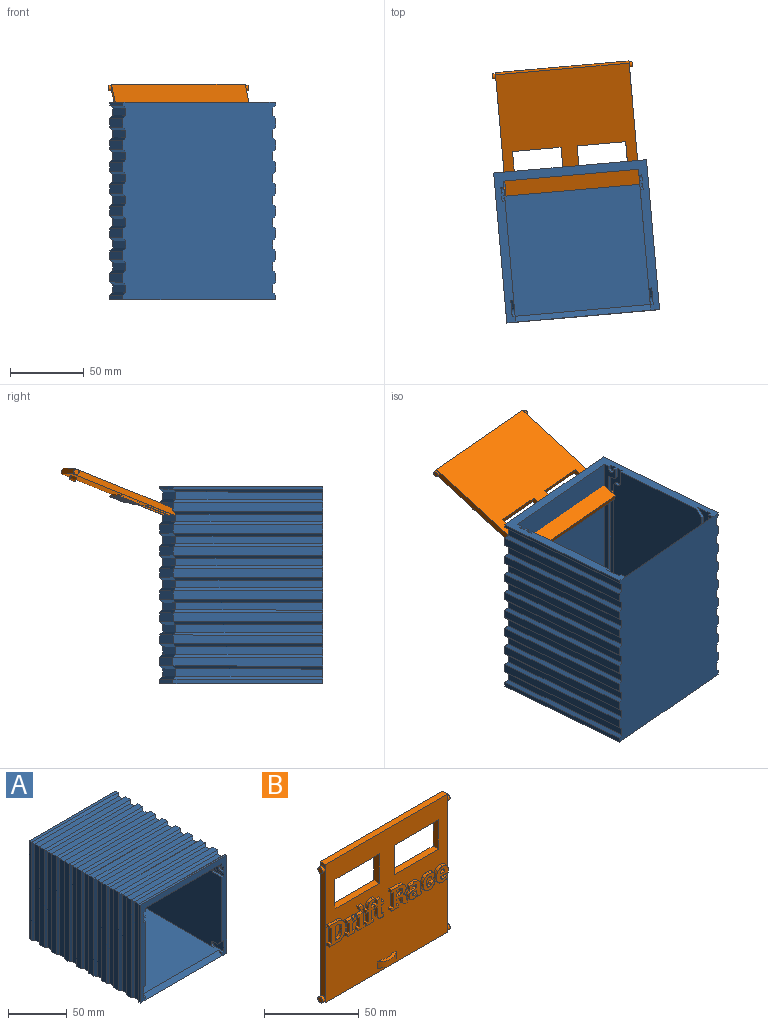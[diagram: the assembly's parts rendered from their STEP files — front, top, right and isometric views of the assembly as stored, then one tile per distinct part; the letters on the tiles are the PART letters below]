
ASSEMBLY  parts=2 mates=1
PART A: 160 faces, bbox 104x134x102 mm
  f0: plane 4x4mm, normal (-1,0,0), area 8mm2, adj f1,f32,f37
  f1: plane 104x102mm, normal (0,-1,0), area 1700mm2, adj f0,f2,f30,f32,f33,f34,f35,f38
  f2: plane 130x92mm, normal (1,0,0), area 11415.9mm2, adj f1,f32,f34,f36,f38,f39,f41,f42
  f3: plane 100x5mm, normal (0,0,1), area 500mm2, adj f12,f21,f134,f135
  f4: plane 100x5mm, normal (0,0,1), area 500mm2, adj f20,f22,f136,f137
  f5: plane 100x5mm, normal (0,0,1), area 500mm2, adj f19,f23,f138,f139
  f6: plane 100x5mm, normal (0,0,1), area 500mm2, adj f18,f24,f140,f141
  f7: plane 100x5mm, normal (0,0,1), area 500mm2, adj f17,f25,f142,f143
  f8: plane 100x5mm, normal (0,0,1), area 500mm2, adj f16,f26,f144,f145
  f9: plane 100x5mm, normal (0,0,1), area 500mm2, adj f13,f29,f150,f151
  f10: plane 100x5mm, normal (0,0,1), area 500mm2, adj f15,f27,f146,f147
  f11: plane 100x5mm, normal (0,0,1), area 500mm2, adj f14,f28,f148,f149
  f12: plane 100x5mm, normal (1,0,0), area 500mm2, adj f3,f30,f122,f123
  f13: plane 100x5mm, normal (1,0,0), area 500mm2, adj f9,f30,f106,f107
  f14: plane 100x5mm, normal (1,0,0), area 500mm2, adj f11,f30,f108,f109
  f15: plane 100x5mm, normal (1,0,0), area 500mm2, adj f10,f30,f110,f111
  f16: plane 100x5mm, normal (1,0,0), area 500mm2, adj f8,f30,f112,f113
  f17: plane 100x5mm, normal (1,0,0), area 500mm2, adj f7,f30,f114,f115
  f18: plane 100x5mm, normal (1,0,0), area 500mm2, adj f6,f30,f116,f117
  f19: plane 100x5mm, normal (1,0,0), area 500mm2, adj f5,f30,f118,f119
  f20: plane 100x5mm, normal (1,0,0), area 500mm2, adj f4,f30,f120,f121
  f21: plane 100x5mm, normal (-1,0,0), area 500mm2, adj f3,f30,f79,f80
  f22: plane 100x5mm, normal (-1,0,0), area 500mm2, adj f4,f30,f81,f82
  f23: plane 100x5mm, normal (-1,0,0), area 500mm2, adj f5,f30,f83,f84
  f24: plane 100x5mm, normal (-1,0,0), area 500mm2, adj f6,f30,f85,f86
  f25: plane 100x5mm, normal (-1,0,0), area 500mm2, adj f7,f30,f87,f88
  f26: plane 100x5mm, normal (-1,0,0), area 500mm2, adj f8,f30,f89,f90
  f27: plane 100x5mm, normal (-1,0,0), area 500mm2, adj f10,f30,f91,f92
  f28: plane 100x5mm, normal (-1,0,0), area 500mm2, adj f11,f30,f93,f94
  f29: plane 100x5mm, normal (-1,0,0), area 500mm2, adj f9,f30,f78,f95
  f30: plane 134x104mm, normal (0,0,-1), area 13684mm2, adj f1,f12,f13,f14,f15,f16,f17,f18
  f31: plane 104x102mm, normal (0,1,0), area 10608mm2, adj f30,f68,f104,f126
  f32: plane 130x96mm, normal (0,0,1), area 11632mm2, adj f0,f1,f2,f33,f35,f36,f37,f153
  f33: plane 4x4mm, normal (1,0,0), area 8mm2, adj f1,f32,f37
  f34: plane 130x92mm, normal (0,0,-1), area 11960mm2, adj f1,f2,f35,f36
  f35: plane 130x92mm, normal (-1,0,0), area 11431.9mm2, adj f1,f32,f34,f36,f48,f49,f51,f52
  f36: plane 92x92mm, normal (0,-1,0), area 8464mm2, adj f2,f32,f34,f35
  f37: plane 92x4mm, normal (0,-0.71,0.71), area 520.4mm2, adj f0,f30,f32,f33
  f38: plane 2x2mm, normal (0,0,1), area 4mm2, adj f1,f2,f40,f67
  f39: plane 2x2mm, normal (0,0,-1), area 4mm2, adj f1,f2,f40,f67
  f40: plane 4x4mm, normal (1,0,0), area 14.3mm2, adj f1,f38,f39,f67
  f41: plane 2x2mm, normal (0,-1,0), area 4mm2, adj f2,f47,f64,f65
  f42: plane 89x2mm, normal (0,0,1), area 178mm2, adj f2,f47,f65,f66
  f43: plane 95x2mm, normal (0,0,-1), area 190mm2, adj f2,f44,f47,f66
  f44: plane 4x2mm, normal (0,1,0), area 8mm2, adj f2,f43,f47,f63
  f45: plane 6x2mm, normal (0,0,-1), area 12mm2, adj f1,f2,f47,f63
  f46: plane 10x2mm, normal (0,0,1), area 20mm2, adj f1,f2,f47,f64
  f47: plane 105x10mm, normal (1,0,0), area 443.1mm2, adj f1,f41,f42,f43,f44,f45,f46,f63
  f48: plane 2x2mm, normal (0,0,-1), area 4mm2, adj f1,f35,f50,f62
  f49: plane 2x2mm, normal (0,0,1), area 4mm2, adj f1,f35,f50,f62
  f50: plane 4x4mm, normal (-1,0,0), area 14.3mm2, adj f1,f48,f49,f62
  f51: plane 4x2mm, normal (0,1,0), area 8mm2, adj f35,f52,f57,f60
  f52: plane 91x2mm, normal (0,0,-1), area 182mm2, adj f35,f51,f57,f58
  f53: plane 85x2mm, normal (0,0,1), area 170mm2, adj f35,f57,f58,f59
  f54: plane 2x2mm, normal (0,-1,0), area 4mm2, adj f35,f57,f59,f61
  f55: plane 10x2mm, normal (0,0,1), area 20mm2, adj f1,f35,f57,f61
  f56: plane 6x2mm, normal (0,0,-1), area 12mm2, adj f1,f35,f57,f60
  f57: plane 101x10mm, normal (-1,0,0), area 427.1mm2, adj f1,f51,f52,f53,f54,f55,f56,f58
  f58: cylinder r=2mm len=4mm, axis (-1,0,0), area 12.6mm2, adj f35,f52,f53,f57
  f59: cylinder r=2mm len=2mm, axis (1,0,0), area 6.3mm2, adj f35,f53,f54,f57
  f60: cylinder r=2mm len=2mm, axis (-1,0,0), area 6.3mm2, adj f35,f51,f56,f57
  f61: cylinder r=2mm len=2mm, axis (1,0,0), area 6.3mm2, adj f35,f54,f55,f57
  f62: cylinder r=2mm len=4mm, axis (1,0,0), area 12.6mm2, adj f35,f48,f49,f50
  f63: cylinder r=2mm len=2mm, axis (-1,0,0), area 6.3mm2, adj f2,f44,f45,f47
  f64: cylinder r=2mm len=2mm, axis (-1,0,0), area 6.3mm2, adj f2,f41,f46,f47
  f65: cylinder r=2mm len=2mm, axis (-1,0,0), area 6.3mm2, adj f2,f41,f42,f47
  f66: cylinder r=2mm len=4mm, axis (-1,0,0), area 12.6mm2, adj f2,f42,f43,f47
  f67: cylinder r=2mm len=4mm, axis (-1,0,0), area 12.6mm2, adj f2,f38,f39,f40
  f68: plane 102x3mm, normal (-1,0,0), area 306mm2, adj f30,f31,f78,f126
  f69: plane 102x6mm, normal (-1,0,0), area 612mm2, adj f30,f94,f95,f124
  f70: plane 102x6mm, normal (-1,0,0), area 612mm2, adj f30,f92,f93,f125
  f71: plane 102x6mm, normal (-1,0,0), area 612mm2, adj f30,f90,f91,f127
  f72: plane 102x6mm, normal (-1,0,0), area 612mm2, adj f30,f88,f89,f128
  f73: plane 102x6mm, normal (-1,0,0), area 612mm2, adj f30,f86,f87,f129
  f74: plane 102x6mm, normal (-1,0,0), area 612mm2, adj f30,f84,f85,f130
  f75: plane 102x6mm, normal (-1,0,0), area 612mm2, adj f30,f82,f83,f131
  f76: plane 102x6mm, normal (-1,0,0), area 612mm2, adj f30,f80,f81,f132
  f77: plane 102x2mm, normal (-1,0,0), area 204mm2, adj f1,f30,f79,f133
  f78: plane 102x2mm, normal (-0.71,-0.71,0), area 285.7mm2, adj f29,f30,f68,f151
  f79: plane 102x2mm, normal (-0.71,0.71,0), area 285.7mm2, adj f21,f30,f77,f134
  f80: plane 102x2mm, normal (-0.71,-0.71,0), area 285.7mm2, adj f21,f30,f76,f135
  f81: plane 102x2mm, normal (-0.71,0.71,0), area 285.7mm2, adj f22,f30,f76,f136
  f82: plane 102x2mm, normal (-0.71,-0.71,0), area 285.7mm2, adj f22,f30,f75,f137
  f83: plane 102x2mm, normal (-0.71,0.71,0), area 285.7mm2, adj f23,f30,f75,f138
  f84: plane 102x2mm, normal (-0.71,-0.71,0), area 285.7mm2, adj f23,f30,f74,f139
  f85: plane 102x2mm, normal (-0.71,0.71,0), area 285.7mm2, adj f24,f30,f74,f140
  f86: plane 102x2mm, normal (-0.71,-0.71,0), area 285.7mm2, adj f24,f30,f73,f141
  f87: plane 102x2mm, normal (-0.71,0.71,0), area 285.7mm2, adj f25,f30,f73,f142
  f88: plane 102x2mm, normal (-0.71,-0.71,0), area 285.7mm2, adj f25,f30,f72,f143
  f89: plane 102x2mm, normal (-0.71,0.71,0), area 285.7mm2, adj f26,f30,f72,f144
  f90: plane 102x2mm, normal (-0.71,-0.71,0), area 285.7mm2, adj f26,f30,f71,f145
  f91: plane 102x2mm, normal (-0.71,0.71,0), area 285.7mm2, adj f27,f30,f71,f146
  f92: plane 102x2mm, normal (-0.71,-0.71,0), area 285.7mm2, adj f27,f30,f70,f147
  f93: plane 102x2mm, normal (-0.71,0.71,0), area 285.7mm2, adj f28,f30,f70,f148
  f94: plane 102x2mm, normal (-0.71,-0.71,0), area 285.7mm2, adj f28,f30,f69,f149
  f95: plane 102x2mm, normal (-0.71,0.71,0), area 285.7mm2, adj f29,f30,f69,f150
  f96: plane 102x6mm, normal (1,0,0), area 612mm2, adj f30,f121,f122,f132
  f97: plane 102x6mm, normal (1,0,0), area 612mm2, adj f30,f119,f120,f131
  f98: plane 102x6mm, normal (1,0,0), area 612mm2, adj f30,f117,f118,f130
  f99: plane 102x6mm, normal (1,0,0), area 612mm2, adj f30,f115,f116,f129
  f100: plane 102x6mm, normal (1,0,0), area 612mm2, adj f30,f113,f114,f128
  f101: plane 102x6mm, normal (1,0,0), area 612mm2, adj f30,f111,f112,f127
  f102: plane 102x6mm, normal (1,0,0), area 612mm2, adj f30,f109,f110,f125
  f103: plane 102x6mm, normal (1,0,0), area 612mm2, adj f30,f106,f108,f124
  f104: plane 102x3mm, normal (1,0,0), area 306mm2, adj f30,f31,f107,f126
  f105: plane 102x2mm, normal (1,0,0), area 204mm2, adj f1,f30,f123,f133
  f106: plane 102x2mm, normal (0.71,0.71,0), area 285.7mm2, adj f13,f30,f103,f150
  f107: plane 102x2mm, normal (0.71,-0.71,0), area 285.7mm2, adj f13,f30,f104,f151
  f108: plane 102x2mm, normal (0.71,-0.71,0), area 285.7mm2, adj f14,f30,f103,f149
  f109: plane 102x2mm, normal (0.71,0.71,0), area 285.7mm2, adj f14,f30,f102,f148
  f110: plane 102x2mm, normal (0.71,-0.71,0), area 285.7mm2, adj f15,f30,f102,f147
  f111: plane 102x2mm, normal (0.71,0.71,0), area 285.7mm2, adj f15,f30,f101,f146
  f112: plane 102x2mm, normal (0.71,-0.71,0), area 285.7mm2, adj f16,f30,f101,f145
  f113: plane 102x2mm, normal (0.71,0.71,0), area 285.7mm2, adj f16,f30,f100,f144
  f114: plane 102x2mm, normal (0.71,-0.71,0), area 285.7mm2, adj f17,f30,f100,f143
  f115: plane 102x2mm, normal (0.71,0.71,0), area 285.7mm2, adj f17,f30,f99,f142
  f116: plane 102x2mm, normal (0.71,-0.71,0), area 285.7mm2, adj f18,f30,f99,f141
  f117: plane 102x2mm, normal (0.71,0.71,0), area 285.7mm2, adj f18,f30,f98,f140
  f118: plane 102x2mm, normal (0.71,-0.71,0), area 285.7mm2, adj f19,f30,f98,f139
  f119: plane 102x2mm, normal (0.71,0.71,0), area 285.7mm2, adj f19,f30,f97,f138
  f120: plane 102x2mm, normal (0.71,-0.71,0), area 285.7mm2, adj f20,f30,f97,f137
  f121: plane 102x2mm, normal (0.71,0.71,0), area 285.7mm2, adj f20,f30,f96,f136
  f122: plane 102x2mm, normal (0.71,-0.71,0), area 285.7mm2, adj f12,f30,f96,f135
  f123: plane 102x2mm, normal (0.71,0.71,0), area 285.7mm2, adj f12,f30,f105,f134
  f124: plane 104x6mm, normal (0,0,1), area 624mm2, adj f69,f103,f149,f150
  f125: plane 104x6mm, normal (0,0,1), area 624mm2, adj f70,f102,f147,f148
  f126: plane 104x3mm, normal (0,0,1), area 312mm2, adj f31,f68,f104,f151
  f127: plane 104x6mm, normal (0,0,1), area 624mm2, adj f71,f101,f145,f146
  f128: plane 104x6mm, normal (0,0,1), area 624mm2, adj f72,f100,f143,f144
  f129: plane 104x6mm, normal (0,0,1), area 624mm2, adj f73,f99,f141,f142
  f130: plane 104x6mm, normal (0,0,1), area 624mm2, adj f74,f98,f139,f140
  f131: plane 104x6mm, normal (0,0,1), area 624mm2, adj f75,f97,f137,f138
  f132: plane 104x6mm, normal (0,0,1), area 624mm2, adj f76,f96,f135,f136
  f133: plane 104x2mm, normal (0,0,1), area 208mm2, adj f1,f77,f105,f134
  f134: plane 104x2mm, normal (0,0.71,0.71), area 288.5mm2, adj f3,f79,f123,f133
  f135: plane 104x2mm, normal (0,-0.71,0.71), area 288.5mm2, adj f3,f80,f122,f132
  f136: plane 104x2mm, normal (0,0.71,0.71), area 288.5mm2, adj f4,f81,f121,f132
  f137: plane 104x2mm, normal (0,-0.71,0.71), area 288.5mm2, adj f4,f82,f120,f131
  f138: plane 104x2mm, normal (0,0.71,0.71), area 288.5mm2, adj f5,f83,f119,f131
  f139: plane 104x2mm, normal (0,-0.71,0.71), area 288.5mm2, adj f5,f84,f118,f130
  f140: plane 104x2mm, normal (0,0.71,0.71), area 288.5mm2, adj f6,f85,f117,f130
  f141: plane 104x2mm, normal (0,-0.71,0.71), area 288.5mm2, adj f6,f86,f116,f129
  f142: plane 104x2mm, normal (0,0.71,0.71), area 288.5mm2, adj f7,f87,f115,f129
  f143: plane 104x2mm, normal (0,-0.71,0.71), area 288.5mm2, adj f7,f88,f114,f128
  f144: plane 104x2mm, normal (0,0.71,0.71), area 288.5mm2, adj f8,f89,f113,f128
  f145: plane 104x2mm, normal (0,-0.71,0.71), area 288.5mm2, adj f8,f90,f112,f127
  f146: plane 104x2mm, normal (0,0.71,0.71), area 288.5mm2, adj f10,f91,f111,f127
  f147: plane 104x2mm, normal (0,-0.71,0.71), area 288.5mm2, adj f10,f92,f110,f125
  f148: plane 104x2mm, normal (0,0.71,0.71), area 288.5mm2, adj f11,f93,f109,f125
  f149: plane 104x2mm, normal (0,-0.71,0.71), area 288.5mm2, adj f11,f94,f108,f124
  f150: plane 104x2mm, normal (0,0.71,0.71), area 288.5mm2, adj f9,f95,f106,f124
  f151: plane 104x2mm, normal (0,-0.71,0.71), area 288.5mm2, adj f9,f78,f107,f126
  f152: plane 5x2mm, normal (0,0,-1), area 10mm2, adj f2,f153,f157,f159
  f153: plane 13x11mm, normal (1,0,0), area 86.6mm2, adj f1,f32,f152,f157,f159
  f154: plane 5x2mm, normal (0,0,-1), area 10mm2, adj f35,f155,f156,f158
  f155: plane 13x11mm, normal (-1,0,0), area 86.6mm2, adj f1,f32,f154,f156,f158
  f156: cylinder r=3mm len=6mm, axis (-1,0,0), area 18.8mm2, adj f32,f35,f154,f155
  f157: cylinder r=3mm len=6mm, axis (-1,0,0), area 18.8mm2, adj f2,f32,f152,f153
  f158: plane 5x5mm, normal (0,-0.71,-0.71), area 14.1mm2, adj f1,f35,f154,f155
  f159: plane 5x5mm, normal (0,-0.71,-0.71), area 14.1mm2, adj f1,f2,f152,f153
PART B: 254 faces, bbox 95x7x89 mm
  f0: plane 14x3mm, normal (0,0,-1), area 23.9mm2, adj f2,f251,f252
  f1: plane 14x3mm, normal (0,0,1), area 23.9mm2, adj f2,f251,f252
  f2: plane 91x89mm, normal (0,-1,0), area 6218mm2, adj f0,f1,f4,f5,f6,f22,f23,f24
  f3: plane 91x89mm, normal (0,1,0), area 6845mm2, adj f4,f5,f6,f243,f244,f245,f246,f247
  f4: plane 89x4mm, normal (1,0,0), area 336.8mm2, adj f2,f3,f6,f9,f13,f253
  f5: plane 89x4mm, normal (-1,0,0), area 336.8mm2, adj f2,f3,f6,f8,f12,f253
  f6: plane 91x4mm, normal (0,0,-1), area 364mm2, adj f2,f3,f4,f5
  f7: plane 3.5x3.5mm, normal (-1,0,0), area 9.6mm2, adj f8
  f8: cylinder r=1.75mm len=3.5mm, axis (1,0,0), area 22mm2, adj f5,f7
  f9: cylinder r=1.75mm len=3.5mm, axis (1,0,0), area 22mm2, adj f4,f10
  f10: plane 3.5x3.5mm, normal (1,0,0), area 9.6mm2, adj f9
  f11: plane 3.5x3.5mm, normal (-1,0,0), area 9.6mm2, adj f12
  f12: cylinder r=1.75mm len=3.5mm, axis (1,0,0), area 22mm2, adj f5,f11
  f13: cylinder r=1.75mm len=3.5mm, axis (1,0,0), area 22mm2, adj f4,f14
  f14: plane 3.5x3.5mm, normal (1,0,0), area 9.6mm2, adj f13
  f15: plane 9.33x2mm, normal (1,0,0), area 18.7mm2, adj f16,f34,f35,f36
  f16: plane 2x1.79mm, normal (0,0,-1), area 3.6mm2, adj f15,f17,f35,f36
  f17: extruded ~2.28x2mm, area 5.1mm2, adj f16,f18,f35,f36
  f18: extruded ~2.55x2mm, area 5.5mm2, adj f17,f19,f35,f36
  f19: plane 2.25x2mm, normal (-1,0,0), area 4.5mm2, adj f18,f20,f35,f36
  f20: extruded ~2.57x2mm, area 5.5mm2, adj f19,f21,f35,f36
  f21: extruded ~2.28x2mm, area 5.1mm2, adj f20,f34,f35,f36
  f22: extruded ~4.08x2mm, area 9mm2, adj f2,f23,f33,f35
  f23: plane 6.07x2mm, normal (0,0,1), area 12.1mm2, adj f2,f22,f24,f35
  f24: plane 2x1.63mm, normal (-1,0,0), area 3.3mm2, adj f2,f23,f25,f35
  f25: plane 2x1.44mm, normal (-0.19,0,-0.98), area 2.9mm2, adj f2,f24,f26,f35
  f26: plane 9.68x2mm, normal (-1,0,0), area 19.4mm2, adj f2,f25,f27,f35
  f27: plane 2x1.44mm, normal (-0.19,0,0.98), area 2.9mm2, adj f2,f26,f28,f35
  f28: plane 2x1.62mm, normal (-1,0,0), area 3.2mm2, adj f2,f27,f29,f35
  f29: plane 6.07x2mm, normal (0,0,-1), area 12.1mm2, adj f2,f28,f30,f35
  f30: extruded ~4.08x2mm, area 9mm2, adj f2,f29,f31,f35
  f31: extruded ~4.05x2mm, area 9mm2, adj f2,f30,f32,f35
  f32: plane 2.23x2mm, normal (1,0,0), area 4.5mm2, adj f2,f31,f33,f35
  f33: extruded ~4.05x2mm, area 9mm2, adj f2,f22,f32,f35
  f34: plane 2x1.79mm, normal (0,0,1), area 3.6mm2, adj f15,f21,f35,f36
  f35: plane 13.49x11.75mm, normal (0,-1,0), area 90mm2, adj f15,f16,f17,f18,f19,f20,f21,f22
  f36: plane 9.33x4.89mm, normal (0,-1,0), area 41.5mm2, adj f15,f16,f17,f18,f19,f20,f21,f34
  f37: plane 2x1.3mm, normal (-0.21,0,0.98), area 2.7mm2, adj f2,f38,f55,f56
  f38: plane 2x1.62mm, normal (-1,0,0), area 3.2mm2, adj f2,f37,f39,f56
  f39: plane 5.3x2mm, normal (0,0,-1), area 10.6mm2, adj f2,f38,f40,f56
  f40: plane 2x1.62mm, normal (1,0,0), area 3.2mm2, adj f2,f39,f41,f56
  f41: plane 2x1.3mm, normal (0.21,0,0.98), area 2.7mm2, adj f2,f40,f42,f56
  f42: plane 4.87x2mm, normal (1,0,0), area 9.7mm2, adj f2,f41,f43,f56
  f43: extruded ~2x0.66mm, area 1.8mm2, adj f2,f42,f44,f56
  f44: extruded ~2x0.98mm, area 2mm2, adj f2,f43,f45,f56
  f45: plane 2x1.11mm, normal (-0.02,0,-1), area 2.2mm2, adj f2,f44,f46,f56
  f46: plane 2.46x2mm, normal (0.99,0,-0.12), area 5mm2, adj f2,f45,f47,f56
  f47: extruded ~2x0.39mm, area 0.8mm2, adj f2,f46,f48,f56
  f48: extruded ~2x0.45mm, area 0.9mm2, adj f2,f47,f49,f56
  f49: extruded ~2x1.29mm, area 2.8mm2, adj f2,f48,f50,f56
  f50: extruded ~2x1.21mm, area 3.1mm2, adj f2,f49,f51,f56
  f51: plane 2x1.46mm, normal (1,0,0.08), area 2.9mm2, adj f2,f50,f52,f56
  f52: plane 3.95x2mm, normal (0,0,1), area 7.9mm2, adj f2,f51,f53,f56
  f53: plane 2x1.63mm, normal (-1,0,0), area 3.3mm2, adj f2,f52,f54,f56
  f54: plane 2x1.44mm, normal (-0.19,0,-0.98), area 2.9mm2, adj f2,f53,f55,f56
  f55: plane 6.22x2mm, normal (-1,0,0), area 12.4mm2, adj f2,f37,f54,f56
  f56: plane 10.21x7.12mm, normal (0,-1,0), area 40.7mm2, adj f37,f38,f39,f40,f41,f42,f43,f44
  f57: plane 2x1.3mm, normal (-0.21,0,0.98), area 2.7mm2, adj f2,f58,f66,f67
  f58: plane 2x1.62mm, normal (-1,0,0), area 3.2mm2, adj f2,f57,f59,f67
  f59: plane 5.31x2mm, normal (0,0,-1), area 10.6mm2, adj f2,f58,f60,f67
  f60: plane 2x1.62mm, normal (1,0,0), area 3.2mm2, adj f2,f59,f61,f67
  f61: plane 2x1.3mm, normal (0.21,0,0.98), area 2.7mm2, adj f2,f60,f62,f67
  f62: plane 8.12x2mm, normal (1,0,0), area 16.2mm2, adj f2,f61,f63,f67
  f63: plane 4.15x2mm, normal (0,0,1), area 8.3mm2, adj f2,f62,f64,f67
  f64: plane 2x1.63mm, normal (-1,0,0), area 3.3mm2, adj f2,f63,f65,f67
  f65: plane 2x1.44mm, normal (-0.19,0,-0.98), area 2.9mm2, adj f2,f64,f66,f67
  f66: plane 6.22x2mm, normal (-1,0,0), area 12.4mm2, adj f2,f57,f65,f67
  f67: plane 10.02x5.45mm, normal (0,-1,0), area 34.3mm2, adj f57,f58,f59,f60,f61,f62,f63,f64
  f68: plane 2.71x2mm, normal (0,0,-1), area 5.4mm2, adj f2,f69,f71,f72
  f69: plane 2.03x2mm, normal (1,0,0), area 4.1mm2, adj f2,f68,f70,f72
  f70: plane 2.71x2mm, normal (0,0,1), area 5.4mm2, adj f2,f69,f71,f72
  f71: plane 2.03x2mm, normal (-1,0,0), area 4.1mm2, adj f2,f68,f70,f72
  f72: plane 2.71x2.03mm, normal (0,-1,0), area 5.5mm2, adj f68,f69,f70,f71
  f73: plane 2x1.31mm, normal (-0.21,0,0.98), area 2.7mm2, adj f2,f74,f96,f97
  f74: plane 2x1.62mm, normal (-1,0,0), area 3.2mm2, adj f2,f73,f75,f97
  f75: plane 5.32x2mm, normal (0,0,-1), area 10.6mm2, adj f2,f74,f76,f97
  f76: plane 2x1.62mm, normal (1,0,0), area 3.2mm2, adj f2,f75,f77,f97
  f77: plane 2x1.31mm, normal (0.21,0,0.98), area 2.7mm2, adj f2,f76,f78,f97
  f78: plane 6.23x2mm, normal (1,0,0), area 12.5mm2, adj f2,f77,f79,f97
  f79: plane 2x1.99mm, normal (0,0,-1), area 4mm2, adj f2,f78,f80,f97
  f80: plane 2x1.9mm, normal (1,0,0), area 3.8mm2, adj f2,f79,f81,f97
  f81: plane 2x1.99mm, normal (0,0,1), area 4mm2, adj f2,f80,f82,f97
  f82: plane 2x1.11mm, normal (1,0,0), area 2.2mm2, adj f2,f81,f83,f97
  f83: extruded ~2x1.04mm, area 2.2mm2, adj f2,f82,f84,f97
  f84: extruded ~2x1mm, area 2.2mm2, adj f2,f83,f85,f97
  f85: extruded ~2x0.49mm, area 1mm2, adj f2,f84,f86,f97
  f86: extruded ~2x0.43mm, area 0.9mm2, adj f2,f85,f87,f97
  f87: plane 2.01x2mm, normal (0.99,0,-0.12), area 4mm2, adj f2,f86,f88,f97
  f88: extruded ~2x0.78mm, area 1.6mm2, adj f2,f87,f89,f97
  f89: extruded ~2x0.7mm, area 1.4mm2, adj f2,f88,f90,f97
  f90: extruded ~2.73x2mm, area 5.9mm2, adj f2,f89,f91,f97
  f91: extruded ~2.6x2mm, area 5.7mm2, adj f2,f90,f92,f97
  f92: plane 2x1.11mm, normal (-1,0,0), area 2.2mm2, adj f2,f91,f93,f97
  f93: plane 2x1.49mm, normal (0,0,1), area 3mm2, adj f2,f92,f94,f97
  f94: plane 2x1.9mm, normal (-1,0,0), area 3.8mm2, adj f2,f93,f95,f97
  f95: plane 2x1.49mm, normal (0,0,-1), area 3mm2, adj f2,f94,f96,f97
  f96: plane 6.23x2mm, normal (-1,0,0), area 12.5mm2, adj f2,f73,f95,f97
  f97: plane 14.65x6.68mm, normal (0,-1,0), area 53.8mm2, adj f73,f74,f75,f76,f77,f78,f79,f80
  f98: plane 2.45x2mm, normal (1,0,0), area 4.9mm2, adj f2,f99,f117,f118
  f99: plane 2.7x2mm, normal (0,0,1), area 5.4mm2, adj f2,f98,f100,f118
  f100: plane 2.45x2mm, normal (-1,0,0), area 4.9mm2, adj f2,f99,f101,f118
  f101: plane 2x1.47mm, normal (0,0,1), area 2.9mm2, adj f2,f100,f102,f118
  f102: plane 2x1.9mm, normal (-1,0,0), area 3.8mm2, adj f2,f101,f103,f118
  f103: plane 2x1.47mm, normal (0,0,-1), area 2.9mm2, adj f2,f102,f104,f118
  f104: plane 5.11x2mm, normal (-1,0,0), area 10.2mm2, adj f2,f103,f105,f118
  f105: extruded ~2.44x2mm, area 5.2mm2, adj f2,f104,f106,f118
  f106: extruded ~2.16x2mm, area 4.7mm2, adj f2,f105,f107,f118
  f107: extruded ~2x0.96mm, area 1.9mm2, adj f2,f106,f108,f118
  f108: extruded ~2x0.9mm, area 1.8mm2, adj f2,f107,f109,f118
  f109: plane 2x1.96mm, normal (0.99,0,0.12), area 3.9mm2, adj f2,f108,f110,f118
  f110: extruded ~2x0.47mm, area 1mm2, adj f2,f109,f111,f118
  f111: extruded ~2x0.49mm, area 1mm2, adj f2,f110,f112,f118
  f112: extruded ~2x0.65mm, area 1.4mm2, adj f2,f111,f113,f118
  f113: extruded ~2x0.83mm, area 1.8mm2, adj f2,f112,f114,f118
  f114: plane 5.11x2mm, normal (1,0,0), area 10.2mm2, adj f2,f113,f115,f118
  f115: plane 2x1.76mm, normal (0,0,-1), area 3.5mm2, adj f2,f114,f116,f118
  f116: plane 2x1.9mm, normal (1,0,0), area 3.8mm2, adj f2,f115,f117,f118
  f117: plane 2x1.76mm, normal (0,0,1), area 3.5mm2, adj f2,f98,f116,f118
  f118: plane 12.67x6.24mm, normal (0,-1,0), area 43mm2, adj f98,f99,f100,f101,f102,f103,f104,f105
  f119: plane 2x1.87mm, normal (0,0,1), area 3.7mm2, adj f120,f153,f154,f155
  f120: plane 3.86x2mm, normal (1,0,0), area 7.7mm2, adj f119,f121,f154,f155
  f121: plane 2x1.92mm, normal (0,0,-1), area 3.8mm2, adj f120,f122,f154,f155
  f122: extruded ~2x1.65mm, area 3.6mm2, adj f121,f123,f154,f155
  f123: extruded ~2x1.45mm, area 3.2mm2, adj f122,f124,f154,f155
  f124: extruded ~2x1.39mm, area 3.1mm2, adj f123,f153,f154,f155
  f125: extruded ~3.6x2mm, area 7.7mm2, adj f2,f126,f152,f154
  f126: plane 6.06x2mm, normal (0,0,1), area 12.1mm2, adj f2,f125,f127,f154
  f127: plane 2x1.63mm, normal (-1,0,0), area 3.3mm2, adj f2,f126,f128,f154
  f128: plane 2x1.44mm, normal (-0.19,0,-0.98), area 2.9mm2, adj f2,f127,f129,f154
  f129: plane 9.68x2mm, normal (-1,0,0), area 19.4mm2, adj f2,f128,f130,f154
  f130: plane 2x1.44mm, normal (-0.19,0,0.98), area 2.9mm2, adj f2,f129,f131,f154
  f131: plane 2x1.62mm, normal (-1,0,0), area 3.2mm2, adj f2,f130,f132,f154
  f132: plane 5.59x2mm, normal (0,0,-1), area 11.2mm2, adj f2,f131,f133,f154
  f133: plane 2x1.62mm, normal (1,0,0), area 3.2mm2, adj f2,f132,f134,f154
  f134: plane 2x1.44mm, normal (0.19,0,0.98), area 2.9mm2, adj f2,f133,f135,f154
  f135: plane 3.56x2mm, normal (1,0,0), area 7.1mm2, adj f2,f134,f136,f154
  f136: plane 2.21x2mm, normal (0,0,-1), area 4.4mm2, adj f2,f135,f137,f154
  f137: extruded ~2x1.48mm, area 3.3mm2, adj f2,f136,f138,f154
  f138: extruded ~2x1.54mm, area 3.3mm2, adj f2,f137,f139,f154
  f139: plane 2x0.77mm, normal (-1,0,0), area 1.5mm2, adj f2,f138,f140,f154
  f140: extruded ~2x1.85mm, area 3.9mm2, adj f2,f139,f141,f154
  f141: extruded ~2x1.86mm, area 4.1mm2, adj f2,f140,f142,f154
  f142: plane 2x1.4mm, normal (0,0,-1), area 2.8mm2, adj f2,f141,f143,f154
  f143: plane 2x1.63mm, normal (1,0,0), area 3.3mm2, adj f2,f142,f144,f154
  f144: plane 2x0.33mm, normal (0.14,0,0.99), area 0.7mm2, adj f2,f143,f145,f154
  f145: extruded ~2x0.59mm, area 1.3mm2, adj f2,f144,f146,f154
  f146: extruded ~2x0.69mm, area 1.4mm2, adj f2,f145,f147,f154
  f147: plane 2x0.69mm, normal (1,0,0), area 1.4mm2, adj f2,f146,f148,f154
  f148: extruded ~2.04x2mm, area 4.3mm2, adj f2,f147,f149,f154
  f149: extruded ~2x1.72mm, area 4.2mm2, adj f2,f148,f150,f154
  f150: extruded ~2x1.6mm, area 4.1mm2, adj f2,f149,f151,f154
  f151: extruded ~2x1.77mm, area 3.8mm2, adj f2,f150,f152,f154
  f152: extruded ~2.9x2mm, area 6.6mm2, adj f2,f125,f151,f154
  f153: extruded ~2x1.7mm, area 3.6mm2, adj f119,f124,f154,f155
  f154: plane 13.49x12.15mm, normal (0,-1,0), area 94.1mm2, adj f119,f120,f121,f122,f123,f124,f125,f126
  f155: plane 4.13x3.86mm, normal (0,-1,0), area 14.4mm2, adj f119,f120,f121,f122,f123,f124,f153
  f156: extruded ~2x1.11mm, area 2.3mm2, adj f157,f190,f191,f192
  f157: extruded ~2x0.91mm, area 2mm2, adj f156,f158,f191,f192
  f158: extruded ~2x0.8mm, area 1.8mm2, adj f157,f159,f191,f192
  f159: extruded ~2x0.97mm, area 2.2mm2, adj f158,f160,f191,f192
  f160: extruded ~2x1.3mm, area 2.8mm2, adj f159,f161,f191,f192
  f161: plane 2x1.38mm, normal (0,0,-1), area 2.8mm2, adj f160,f162,f191,f192
  f162: plane 2x1.53mm, normal (-1,0,0), area 3.1mm2, adj f161,f190,f191,f192
  f163: extruded ~2x0.51mm, area 1.1mm2, adj f2,f164,f189,f191
  f164: plane 3.12x2mm, normal (0,0,-1), area 6.2mm2, adj f2,f163,f165,f191
  f165: plane 2x1.62mm, normal (1,0,0), area 3.2mm2, adj f2,f164,f166,f191
  f166: plane 2x0.82mm, normal (0.13,0,0.99), area 1.7mm2, adj f2,f165,f167,f191
  f167: extruded ~2x0.39mm, area 0.8mm2, adj f2,f166,f168,f191
  f168: extruded ~2x0.44mm, area 0.9mm2, adj f2,f167,f169,f191
  f169: plane 4.14x2mm, normal (1,0,0), area 8.3mm2, adj f2,f168,f170,f191
  f170: extruded ~2.6x2mm, area 5.9mm2, adj f2,f169,f171,f191
  f171: extruded ~3.03x2mm, area 6.4mm2, adj f2,f170,f172,f191
  f172: extruded ~2.09x2mm, area 4.3mm2, adj f2,f171,f173,f191
  f173: extruded ~2x1.7mm, area 3.8mm2, adj f2,f172,f174,f191
  f174: plane 2.22x2mm, normal (-1,0,0), area 4.4mm2, adj f2,f173,f175,f191
  f175: plane 2.04x2mm, normal (0,0,-1), area 4.1mm2, adj f2,f174,f176,f191
  f176: plane 2x1.07mm, normal (0.99,0,-0.16), area 2.2mm2, adj f2,f175,f177,f191
  f177: extruded ~2x0.58mm, area 1.3mm2, adj f2,f176,f178,f191
  f178: extruded ~2x0.83mm, area 1.7mm2, adj f2,f177,f179,f191
  f179: extruded ~2x1.23mm, area 2.7mm2, adj f2,f178,f180,f191
  f180: extruded ~2x1.12mm, area 2.5mm2, adj f2,f179,f181,f191
  f181: plane 2x0.98mm, normal (-1,0,0), area 2mm2, adj f2,f180,f182,f191
  f182: plane 2x1.38mm, normal (0,0,1), area 2.8mm2, adj f2,f181,f183,f191
  f183: extruded ~3.32x2mm, area 6.9mm2, adj f2,f182,f184,f191
  f184: extruded ~2.18x2mm, area 5.1mm2, adj f2,f183,f185,f191
  f185: extruded ~2.18x2mm, area 4.8mm2, adj f2,f184,f186,f191
  f186: extruded ~2.34x2mm, area 5.1mm2, adj f2,f185,f187,f191
  f187: extruded ~2x1.58mm, area 3.3mm2, adj f2,f186,f188,f191
  f188: extruded ~2x1.17mm, area 3mm2, adj f2,f187,f189,f191
  f189: extruded ~2x0.53mm, area 1.1mm2, adj f2,f163,f188,f191
  f190: extruded ~2x0.78mm, area 2.1mm2, adj f156,f162,f191,f192
  f191: plane 10.41x9.4mm, normal (0,-1,0), area 61.9mm2, adj f156,f157,f158,f159,f160,f161,f162,f163
  f192: plane 3.13x2.46mm, normal (0,-1,0), area 6.5mm2, adj f156,f157,f158,f159,f160,f161,f162,f190
  f193: extruded ~2x1.16mm, area 2.5mm2, adj f2,f194,f215,f216
  f194: extruded ~2x1.53mm, area 3.7mm2, adj f2,f193,f195,f216
  f195: extruded ~2.16x2mm, area 4.5mm2, adj f2,f194,f196,f216
  f196: plane 2x0.28mm, normal (1,0,0), area 0.6mm2, adj f2,f195,f197,f216
  f197: extruded ~2.15x2mm, area 4.5mm2, adj f2,f196,f198,f216
  f198: extruded ~2x1.62mm, area 3.8mm2, adj f2,f197,f199,f216
  f199: extruded ~2x0.68mm, area 1.4mm2, adj f2,f198,f200,f216
  f200: extruded ~2x0.5mm, area 1.2mm2, adj f2,f199,f201,f216
  f201: plane 2x1.57mm, normal (-0.96,0,-0.27), area 3.3mm2, adj f2,f200,f202,f216
  f202: plane 2.2x2mm, normal (0,0,-1), area 4.4mm2, adj f2,f201,f203,f216
  f203: plane 2.68x2mm, normal (1,0,0.01), area 5.4mm2, adj f2,f202,f204,f216
  f204: extruded ~2x1.6mm, area 3.8mm2, adj f2,f203,f205,f216
  f205: extruded ~2.18x2mm, area 4.4mm2, adj f2,f204,f206,f216
  f206: extruded ~3.55x2mm, area 7.9mm2, adj f2,f205,f207,f216
  f207: extruded ~3.64x2mm, area 7.9mm2, adj f2,f206,f208,f216
  f208: plane 2x0.28mm, normal (-1,0,0), area 0.6mm2, adj f2,f207,f209,f216
  f209: extruded ~3.64x2mm, area 7.8mm2, adj f2,f208,f210,f216
  f210: extruded ~3.46x2mm, area 7.7mm2, adj f2,f209,f211,f216
  f211: extruded ~2.93x2mm, area 6.3mm2, adj f2,f210,f212,f216
  f212: extruded ~2.55x2mm, area 5.8mm2, adj f2,f211,f213,f216
  f213: plane 2x0.05mm, normal (0.89,0,0.45), area 0.1mm2, adj f2,f212,f214,f216
  f214: plane 2.45x2mm, normal (0,0,1), area 4.9mm2, adj f2,f213,f215,f216
  f215: extruded ~2x1.13mm, area 2.5mm2, adj f2,f193,f214,f216
  f216: plane 10.41x8.78mm, normal (0,-1,0), area 50.8mm2, adj f193,f194,f195,f196,f197,f198,f199,f200
  f217: extruded ~2x1.18mm, area 2.7mm2, adj f218,f240,f241,f242
  f218: extruded ~2x1.22mm, area 2.7mm2, adj f217,f219,f241,f242
  f219: extruded ~2x1.38mm, area 2.9mm2, adj f218,f220,f241,f242
  f220: plane 2x0.24mm, normal (-1,0,0), area 0.5mm2, adj f219,f221,f241,f242
  f221: plane 3.31x2mm, normal (0,0,1), area 6.6mm2, adj f220,f222,f241,f242
  f222: plane 2x0.05mm, normal (0.85,0,0.53), area 0.1mm2, adj f221,f240,f241,f242
  f223: extruded ~3.47x2mm, area 7.7mm2, adj f2,f224,f239,f241
  f224: extruded ~2.2x2mm, area 4.5mm2, adj f2,f223,f225,f241
  f225: extruded ~2x1.61mm, area 3.6mm2, adj f2,f224,f226,f241
  f226: plane 2x1.67mm, normal (0.92,0,0.4), area 3.6mm2, adj f2,f225,f227,f241
  f227: extruded ~2x1.3mm, area 2.8mm2, adj f2,f226,f228,f241
  f228: extruded ~2x1.49mm, area 3mm2, adj f2,f227,f229,f241
  f229: extruded ~2x1.6mm, area 3.6mm2, adj f2,f228,f230,f241
  f230: extruded ~2x1.63mm, area 3.6mm2, adj f2,f229,f231,f241
  f231: plane 2x0.06mm, normal (0.95,0,-0.3), area 0.1mm2, adj f2,f230,f232,f241
  f232: plane 5.99x2mm, normal (0,0,-1), area 12mm2, adj f2,f231,f233,f241
  f233: plane 2x1.47mm, normal (1,0,0), area 2.9mm2, adj f2,f232,f234,f241
  f234: extruded ~3.31x2mm, area 7.2mm2, adj f2,f233,f235,f241
  f235: extruded ~3.15x2mm, area 7mm2, adj f2,f234,f236,f241
  f236: extruded ~3.29x2mm, area 7.4mm2, adj f2,f235,f237,f241
  f237: extruded ~3.68x2mm, area 7.9mm2, adj f2,f236,f238,f241
  f238: plane 2x0.37mm, normal (-1,0,0), area 0.7mm2, adj f2,f237,f239,f241
  f239: extruded ~3.53x2mm, area 7.7mm2, adj f2,f223,f238,f241
  f240: extruded ~2x1.51mm, area 3.2mm2, adj f217,f222,f241,f242
  f241: plane 10.41x8.79mm, normal (0,-1,0), area 59mm2, adj f217,f218,f219,f220,f221,f222,f223,f224
  f242: plane 3.34x2.13mm, normal (0,-1,0), area 5.8mm2, adj f217,f218,f219,f220,f221,f222,f240
  f243: plane 19x4mm, normal (1,0,0), area 76mm2, adj f2,f3,f244,f246
  f244: plane 33x4mm, normal (0,0,1), area 132mm2, adj f2,f3,f243,f245
  f245: plane 19x4mm, normal (-1,0,0), area 76mm2, adj f2,f3,f244,f246
  f246: plane 33x4mm, normal (0,0,-1), area 132mm2, adj f2,f3,f243,f245
  f247: plane 19x4mm, normal (1,0,0), area 76mm2, adj f2,f3,f248,f250
  f248: plane 33x4mm, normal (0,0,1), area 132mm2, adj f2,f3,f247,f249
  f249: plane 19x4mm, normal (-1,0,0), area 76mm2, adj f2,f3,f248,f250
  f250: plane 33x4mm, normal (0,0,-1), area 132mm2, adj f2,f3,f247,f249
  f251: cylinder r=9.67mm len=14mm, axis (0,0,-1), area 62.6mm2, adj f0,f1,f2
  f252: cylinder r=7.67mm len=7.57mm, axis (0,0,-1), area 31.7mm2, adj f0,f1,f2
  f253: plane 91x4mm, normal (0,0,1), area 364mm2, adj f2,f3,f4,f5
PLACE A rot(axis=(-1,-0.04,0.04),90.1deg) t=(111.61,-79.83,-81.01)mm
PLACE B rot(axis=(1,0.04,0.03),112.2deg) t=(105.31,-2.25,48.72)mm
MATE pin_slot B.f8 <-> A.f66  axis (1,0.09,0) through (61.3,-44.16,31.14)mm
